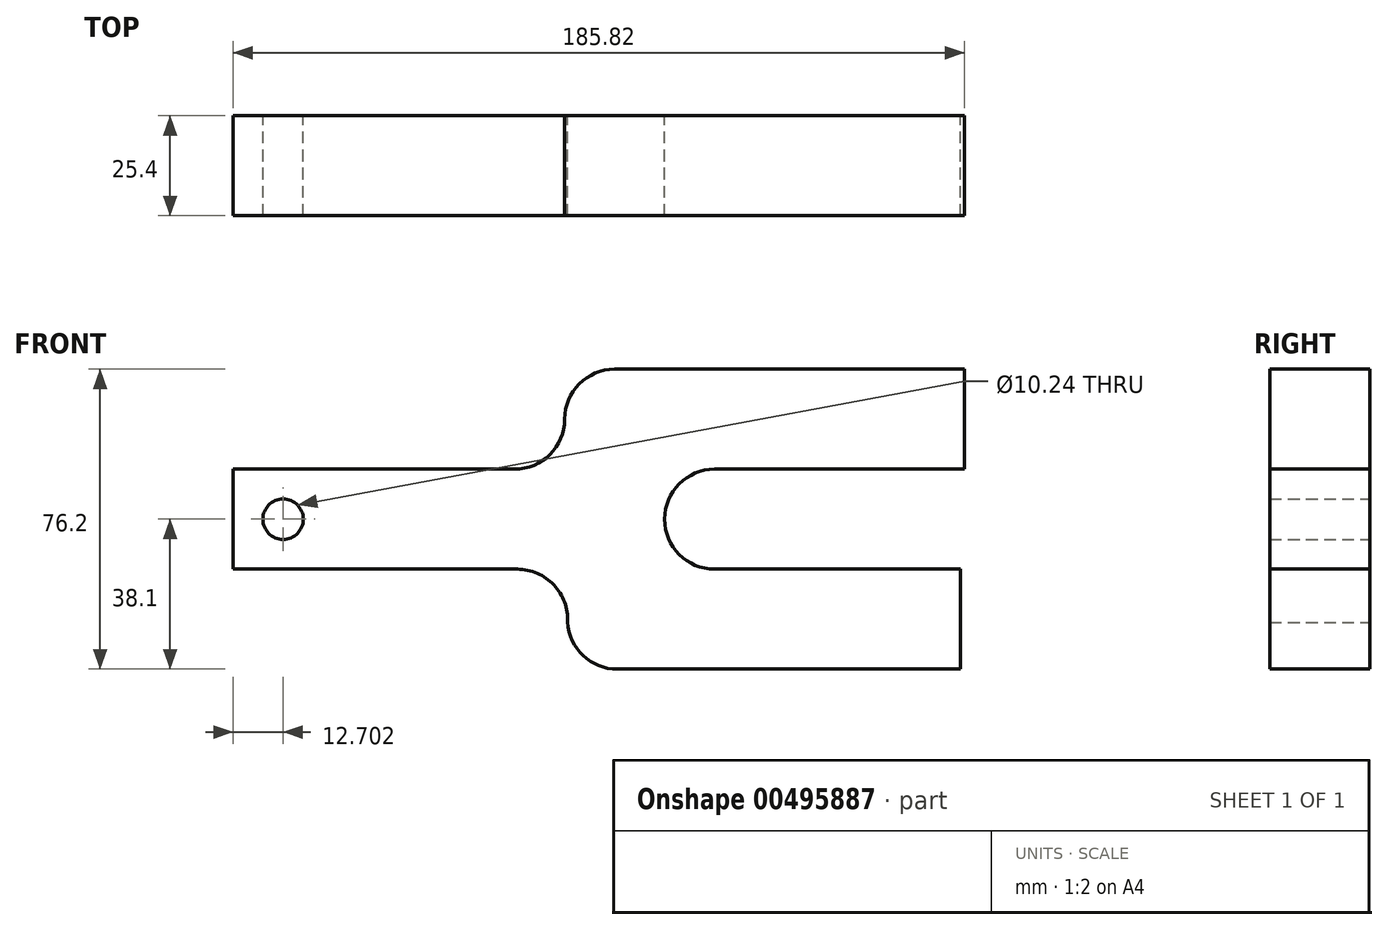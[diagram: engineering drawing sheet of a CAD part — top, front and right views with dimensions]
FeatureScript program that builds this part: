
annotation { "Feature Type Name" : "Feature", "Feature Type Description" : "" }
export const myFeature = defineFeature(function(context is Context, id is Id, definition is map)
    precondition{}
    {
        {
            var Q0;
            Q0=qCreatedBy(makeId("Front.planeOp"),FACE);
            var sketch = newSketch(context, id + "F0", { "sketchPlane" : qUnion([Q0])});
            skLineSegment(sketch, "E0.bottom", {"start": v(-94.76, 0) * mm, "end": v(-167.03, 0) * mm});
            skLineSegment(sketch, "E0.top", {"start": v(-95.5, 25.4) * mm, "end": v(-167.03, 25.4) * mm});
            skLineSegment(sketch, "E0.left", {"start": v(-57.4, 12.7) * mm, "end": v(-57.4, 12.7) * mm});
            skLineSegment(sketch, "E0.right", {"start": v(-167.03, 0) * mm, "end": v(-167.03, 25.4) * mm});
            skPoint(sketch, "E0.middle", {"position": v(-108.64, 12.7) * mm});
            skLineSegment(sketch, "E1.bottom", {"start": v(-44.7, 25.4) * mm, "end": v(18.8, 25.4) * mm});
            skLineSegment(sketch, "E1.top", {"start": v(-70.1, 50.8) * mm, "end": v(18.8, 50.8) * mm});
            skLineSegment(sketch, "E1.left", {"start": v(-82.8, 38.1) * mm, "end": v(-82.8, 38.1) * mm});
            skLineSegment(sketch, "E1.right", {"start": v(18.8, 25.4) * mm, "end": v(18.8, 50.8) * mm});
            skLineSegment(sketch, "E2.bottom", {"start": v(-44.7, 0) * mm, "end": v(17.73, 0) * mm});
            skLineSegment(sketch, "E2.top", {"start": v(-69.4, -25.4) * mm, "end": v(17.73, -25.4) * mm});
            skLineSegment(sketch, "E2.right", {"start": v(17.73, 0) * mm, "end": v(17.73, -25.4) * mm});
            skPoint(sketch, "E3.newPointA", {"position": v(-50.26, 25.4) * mm});
            skPoint(sketch, "E3.newPointB", {"position": v(-82.8, 25.4) * mm});
            skArc(sketch, "E3.filletArc", {"start": v(-95.5, 25.4) * mm, "mid": v(-86.53, 29.12) * mm, "end": v(-82.8, 38.1) * mm});
            skPoint(sketch, "E4.visualSharp", {"position": v(-82.8, 50.8) * mm});
            skArc(sketch, "E4.filletArc", {"start": v(-70.1, 50.8) * mm, "mid": v(-79.09, 47.08) * mm, "end": v(-82.8, 38.1) * mm});
            skPoint(sketch, "E5.newPointA", {"position": v(-50.26, 0) * mm});
            skArc(sketch, "E5.filletArc", {"start": v(-82.08, -13.47) * mm, "mid": v(-85.51, -4) * mm, "end": v(-94.76, 0) * mm});
            skPoint(sketch, "E6.newPointA", {"position": v(-57.4, 22.1) * mm});
            skArc(sketch, "E6.filletArc", {"start": v(-44.7, 25.4) * mm, "mid": v(-53.69, 21.68) * mm, "end": v(-57.4, 12.7) * mm});
            skPoint(sketch, "E7.newPointA", {"position": v(-82.8, 0) * mm});
            skArc(sketch, "E7.filletArc", {"start": v(-57.4, 12.7) * mm, "mid": v(-53.69, 3.72) * mm, "end": v(-44.7, 0) * mm});
            skPoint(sketch, "E8.visualSharp", {"position": v(-82.08, -13.47) * mm});
            skPoint(sketch, "E9.visualSharp", {"position": v(-83.87, -25.4) * mm});
            skArc(sketch, "E9.filletArc", {"start": v(-82.08, -13.47) * mm, "mid": v(-78.11, -21.95) * mm, "end": v(-69.4, -25.4) * mm});
            skCircle(sketch, "E10", {"center": v(-154.33, 12.7) * mm, "radius": 5.12 * mm});
            skSolve(sketch);
        }
        {
            var Q0;
            Q0 = qSketchRegion(id + "F0", true);
            extrude(context, id + "F1", {"entities" : qUnion([Q0]), "endBound" : BoundingType.SYMMETRIC, "depth" : 25.4 * mm});
        }
    });
